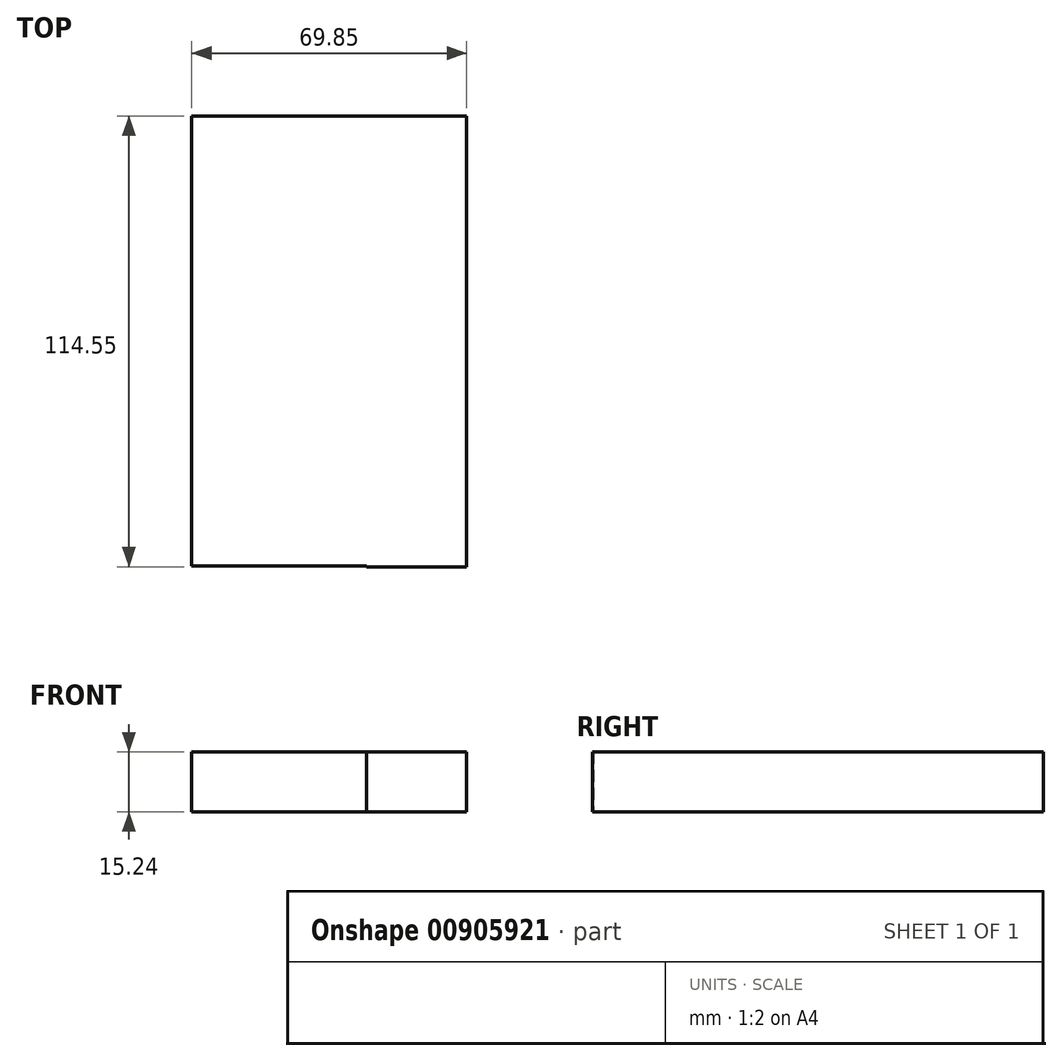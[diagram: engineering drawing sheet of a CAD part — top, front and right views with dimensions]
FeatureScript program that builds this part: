
annotation { "Feature Type Name" : "Feature", "Feature Type Description" : "" }
export const myFeature = defineFeature(function(context is Context, id is Id, definition is map)
    precondition{}
    {
        {
            var Q0;
            Q0=qCreatedBy(makeId("Top.planeOp"),FACE);
            var sketch = newSketch(context, id + "F0", { "sketchPlane" : qUnion([Q0])});
            skLineSegment(sketch, "E0.bottom", {"start": v(-40.72, 63.93) * mm, "end": v(3.73, 63.93) * mm});
            skLineSegment(sketch, "E0.top", {"start": v(-40.72, -50.37) * mm, "end": v(3.73, -50.37) * mm});
            skLineSegment(sketch, "E0.left", {"start": v(-40.72, 63.93) * mm, "end": v(-40.72, -50.37) * mm});
            skLineSegment(sketch, "E0.right", {"start": v(3.73, 63.93) * mm, "end": v(3.73, -50.37) * mm});
            skLineSegment(sketch, "E1.bottom", {"start": v(3.73, 63.93) * mm, "end": v(29.13, 63.93) * mm});
            skLineSegment(sketch, "E1.top", {"start": v(3.73, -50.62) * mm, "end": v(29.13, -50.62) * mm});
            skLineSegment(sketch, "E1.left", {"start": v(3.73, 63.93) * mm, "end": v(3.73, -50.62) * mm});
            skLineSegment(sketch, "E1.right", {"start": v(29.13, 63.93) * mm, "end": v(29.13, -50.62) * mm});
            skSolve(sketch);
        }
        {
            var Q0;
            {var subQ0=sQuery(id+"F0.wireOp",EDGE,"E0.bottom");Q0=makeQuery(id+"F0.imprint","IMPRINT",FACE,{"disambiguationData":[TD([[makeQuery(id+"F0.imprint","IMPRINT",EDGE,{"derivedFrom":subQ0}),-1.0]])]});}
            var Q1;
            {var subQ3=sQuery(id+"F0.wireOp",EDGE,"E1.bottom");Q1=makeQuery(id+"F0.imprint","IMPRINT",FACE,{"disambiguationData":[TD([[makeQuery(id+"F0.imprint","IMPRINT",EDGE,{"derivedFrom":subQ3}),-1.0]])]});}
            extrude(context, id + "F1", {"entities" : qUnion([Q0, Q1]), "depth" : 15.24 * mm, "offsetDistance" : 25.4 * mm});
        }
    });
